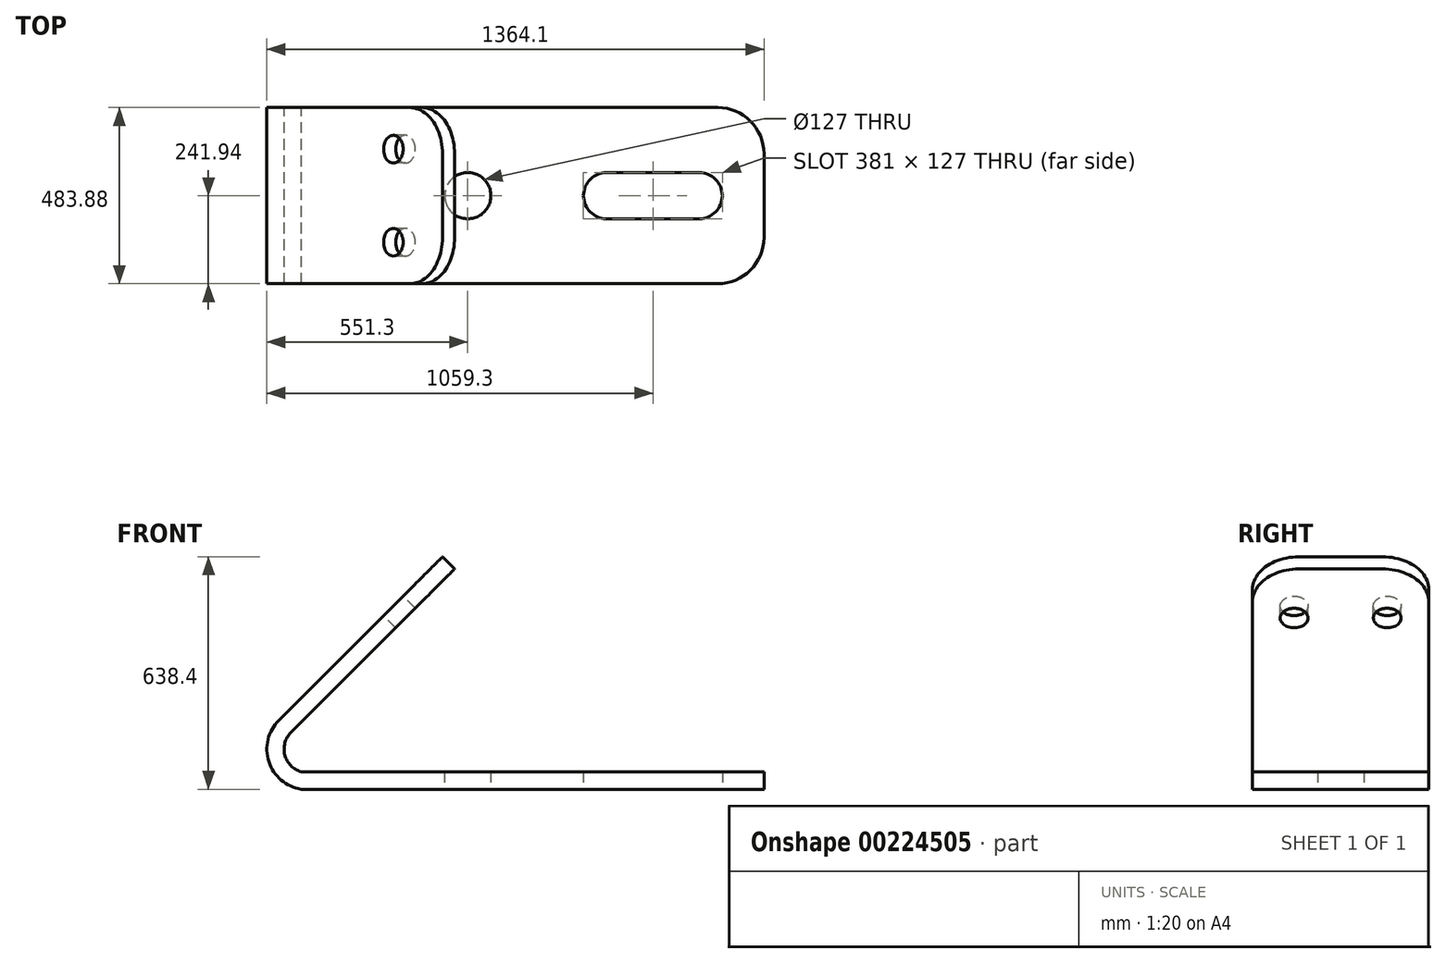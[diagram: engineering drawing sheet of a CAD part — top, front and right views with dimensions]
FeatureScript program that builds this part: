
annotation { "Feature Type Name" : "Feature", "Feature Type Description" : "" }
export const myFeature = defineFeature(function(context is Context, id is Id, definition is map)
    precondition{}
    {
        {
            var Q0;
            Q0=qCreatedBy(makeId("Front.planeOp"),FACE);
            var sketch = newSketch(context, id + "F0", { "sketchPlane" : qUnion([Q0])});
            skLineSegment(sketch, "E0.bottom", {"start": v(0, 0) * mm, "end": v(1270, 0) * mm});
            skLineSegment(sketch, "E0.top", {"start": v(0, 48.26) * mm, "end": v(1270, 48.26) * mm});
            skLineSegment(sketch, "E0.left", {"start": v(0, 0) * mm, "end": v(0, 48.26) * mm});
            skLineSegment(sketch, "E0.right", {"start": v(1270, 0) * mm, "end": v(1270, 48.26) * mm});
            skLineSegment(sketch, "E1", {"start": v(1270, 24.13) * mm, "end": v(-99.6, 24.13) * mm, "construction": true});
            skArc(sketch, "E2", {"start": v(0, 48.26) * mm, "mid": v(-44.83, 94.12) * mm, "end": v(-28, 156) * mm});
            skArc(sketch, "E3", {"start": v(0, 0) * mm, "mid": v(-88.66, 75.9) * mm, "end": v(-61.37, 189.38) * mm});
            skLineSegment(sketch, "E4", {"start": v(-28, 156) * mm, "end": v(421.02, 605.02) * mm});
            skLineSegment(sketch, "E5", {"start": v(-61.37, 189.38) * mm, "end": v(387.64, 638.4) * mm});
            skLineSegment(sketch, "E6", {"start": v(387.64, 638.4) * mm, "end": v(421.02, 605.02) * mm});
            skSolve(sketch);
        }
        {
            var Q0;
            Q0 = qSketchRegion(id + "F0", true);
            extrude(context, id + "F1", {"entities" : qUnion([Q0]), "endBound" : BoundingType.SYMMETRIC, "depth" : 483.87 * mm});
        }
        {
            var Q0;
            Q0=makeQuery(id+"F1.opExtrude","SWEPT_FACE",FACE,{"disambiguationData":[OSD([sQuery(id+"F0.wireOp",EDGE,"E0.bottom")])]});
            var sketch = newSketch(context, id + "F2", { "sketchPlane" : qUnion([Q0])});
            skLineSegment(sketch, "E7", {"start": v(0, 0) * mm, "end": v(1270, 0) * mm, "construction": true});
            skLineSegment(sketch, "E8", {"start": v(1270, 0) * mm, "end": v(1155.7, 0) * mm});
            skArc(sketch, "E9", {"start": v(1155.7, 0) * mm, "mid": v(1137.1, 44.9) * mm, "end": v(1092.2, 63.5) * mm});
            skArc(sketch, "E10", {"start": v(1155.7, 0) * mm, "mid": v(1137.1, -44.9) * mm, "end": v(1092.2, -63.5) * mm});
            skLineSegment(sketch, "E11", {"start": v(1092.2, 63.5) * mm, "end": v(838.2, 63.5) * mm});
            skLineSegment(sketch, "E12", {"start": v(838.2, -63.5) * mm, "end": v(1092.2, -63.5) * mm});
            skArc(sketch, "E13", {"start": v(838.2, -63.5) * mm, "mid": v(793.3, -44.9) * mm, "end": v(774.7, 0) * mm});
            skArc(sketch, "E14", {"start": v(774.7, 0) * mm, "mid": v(793.3, 44.9) * mm, "end": v(838.2, 63.5) * mm});
            skSolve(sketch);
        }
        {
            var Q0;
            Q0 = qSketchRegion(id + "F2", true);
            extrude(context, id + "F3", {"entities" : qUnion([Q0]), "operationType" : NewBodyOperationType.REMOVE, "oppositeDirection" : true, "depth" : 254 * mm});
        }
        {
            var Q0;
            Q0=makeQuery(id+"F1.opExtrude","SWEPT_FACE",FACE,{"disambiguationData":[OSD([sQuery(id+"F0.wireOp",EDGE,"E0.bottom")])]});
            var sketch = newSketch(context, id + "F4", { "sketchPlane" : qUnion([Q0])});
            skLineSegment(sketch, "E15", {"start": v(1270, 241.94) * mm, "end": v(457.2, 241.94) * mm});
            skLineSegment(sketch, "E16", {"start": v(457.2, 241.94) * mm, "end": v(457.2, 0) * mm});
            skCircle(sketch, "E17", {"center": v(457.2, 0) * mm, "radius": 63.5 * mm});
            skSolve(sketch);
        }
        {
            var Q0;
            Q0=makeQuery(id+"F4.imprint","IMPRINT",FACE,{"disambiguationData":[TD([[makeQuery(id+"F4.imprint","IMPRINT",EDGE,{"derivedFrom":sQuery(id+"F4.wireOp",EDGE,"E17")}),1.0]])]});
            extrude(context, id + "F5", {"entities" : qUnion([Q0]), "operationType" : NewBodyOperationType.REMOVE, "oppositeDirection" : true, "depth" : 127 * mm});
        }
        {
            var Q0;
            Q0=makeQuery(id+"F1.opExtrude","SWEPT_FACE",FACE,{"disambiguationData":[OSD([sQuery(id+"F0.wireOp",EDGE,"E5")])]});
            var sketch = newSketch(context, id + "F6", { "sketchPlane" : qUnion([Q0])});
            skLineSegment(sketch, "E18", {"start": v(-241.94, 90.52) * mm, "end": v(-127.76, 90.52) * mm});
            skLineSegment(sketch, "E19", {"start": v(-127.76, 725.52) * mm, "end": v(-127.76, 535.02) * mm});
            skLineSegment(sketch, "E20", {"start": v(0, 725.52) * mm, "end": v(0, -259.8) * mm, "construction": true});
            skPoint(sketch, "E20.endSnap0", {"position": v(0, 725.52) * mm});
            skCircle(sketch, "E21", {"center": v(-127.76, 535.02) * mm, "radius": 38.1 * mm});
            skCircle(sketch, "E22.MirrorC", {"center": v(127.76, 535.02) * mm, "radius": 38.1 * mm});
            skSolve(sketch);
        }
        {
            var Q0;
            Q0 = qSketchRegion(id + "F6", true);
            extrude(context, id + "F7", {"entities" : qUnion([Q0]), "operationType" : NewBodyOperationType.REMOVE, "oppositeDirection" : true, "depth" : 101.6 * mm});
        }
        {
            var Q0;
            Q0=makeQuery(id+"F1.opExtrude","CAP_EDGE",EDGE,{"disambiguationData":[OSD([sQuery(id+"F0.wireOp",EDGE,"E6")])],"isStart":true});
            var Q1;
            Q1=makeQuery(id+"F1.opExtrude","CAP_EDGE",EDGE,{"disambiguationData":[OSD([sQuery(id+"F0.wireOp",EDGE,"E6")])],"isStart":false});
            var Q2;
            Q2=makeQuery(id+"F1.opExtrude","CAP_EDGE",EDGE,{"disambiguationData":[OSD([sQuery(id+"F0.wireOp",EDGE,"E0.right")])],"isStart":false});
            var Q3;
            Q3=makeQuery(id+"F1.opExtrude","CAP_EDGE",EDGE,{"disambiguationData":[OSD([sQuery(id+"F0.wireOp",EDGE,"E0.right")])],"isStart":true});
            fillet(context, id + "F8", {"entities" : qUnion([Q0, Q1, Q2, Q3]), "radius" : 127 * mm, "tangentPropagation" : true, "allowEdgeOverflow" : false});
        }
    });
